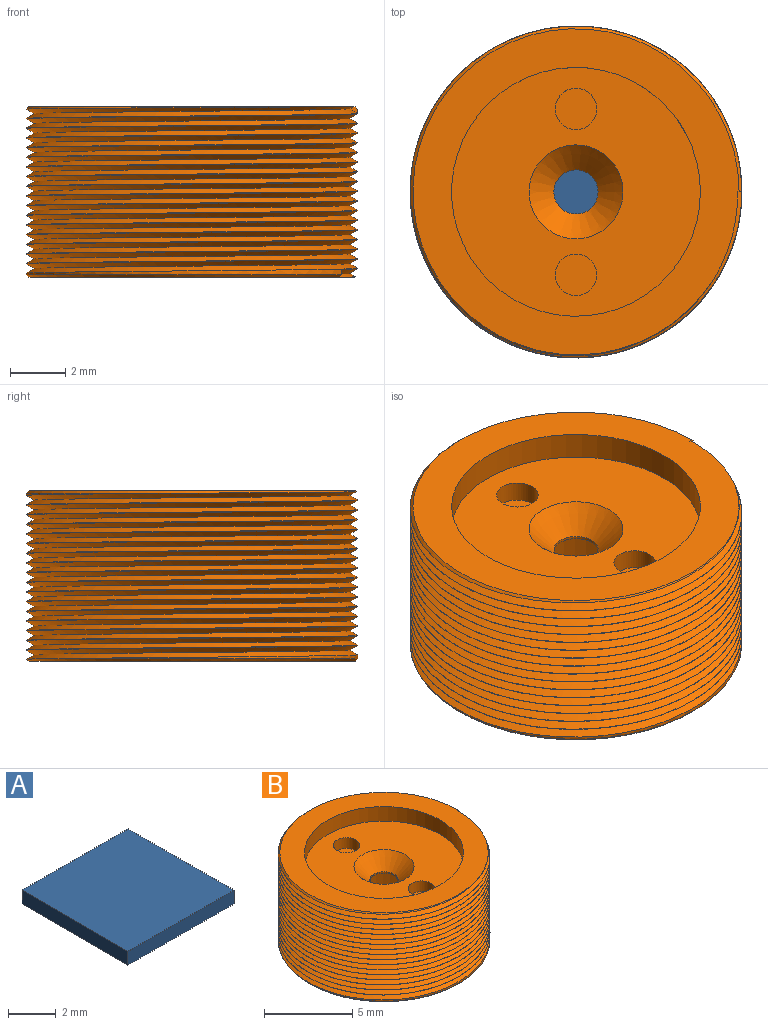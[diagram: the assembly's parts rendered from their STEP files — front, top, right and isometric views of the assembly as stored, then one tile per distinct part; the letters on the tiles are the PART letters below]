
ASSEMBLY  parts=2 mates=1
PART A: 6 faces, bbox 6.3x6.3x0.7 mm
  f0: plane 6.25x0.7mm, normal (0,-1,0), area 4.4mm2, adj f1,f3,f4,f5
  f1: plane 6.25x0.7mm, normal (1,0,0), area 4.4mm2, adj f0,f2,f4,f5
  f2: plane 6.25x0.7mm, normal (0,1,0), area 4.4mm2, adj f1,f3,f4,f5
  f3: plane 6.25x0.7mm, normal (-1,0,0), area 4.4mm2, adj f0,f2,f4,f5
  f4: plane 6.25x6.25mm, normal (0,0,1), area 39.1mm2, adj f0,f1,f2,f3
  f5: plane 6.25x6.25mm, normal (0,0,-1), area 39.1mm2, adj f0,f1,f2,f3
PART B: 21 faces, bbox 12.1x13.9x6.4 mm
  f0: cylinder r=6mm len=12mm, axis (0,0,-1), area 9.1mm2, adj f2,f12,f17,f18,f19,f20
  f1: plane 11.87x11.87mm, normal (0,0,1), area 45.6mm2, adj f2,f4,f17,f20
  f2: cone r=5.9mm half-angle=45deg, axis (0,0,-1), area 3.6mm2, adj f0,f1,f17,f20
  f3: plane 9x9mm, normal (0,0,1), area 51mm2, adj f4,f11,f13,f15
  f4: cylinder r=4.5mm len=9mm, axis (0,0,-1), area 28.3mm2, adj f1,f3
  f5: cylinder r=5mm len=10mm, axis (0,0,1), area 31.4mm2, adj f6,f9
  f6: plane 11.8x11.8mm, normal (0,0,-1), area 30.8mm2, adj f5,f12
  f7: plane 6.5x6.5mm, normal (0,0,-1), area 31.2mm2, adj f8,f10
  f8: cylinder r=3.25mm len=6.5mm, axis (0,0,1), area 64.8mm2, adj f7,f9
  f9: plane 10x10mm, normal (0,0,-1), area 45.4mm2, adj f5,f8
  f10: cylinder r=0.8mm len=1.6mm, axis (0,0,1), area 0.5mm2, adj f7,f11
  f11: cone r=0.8mm half-angle=45deg, axis (0,0,1), area 10mm2, adj f3,f10
  f12: cone r=6mm half-angle=45deg, axis (0,0,1), area 4.2mm2, adj f0,f6,f18,f19
  f13: cylinder r=0.75mm len=1.5mm, axis (0,0,1), area 3.5mm2, adj f3,f14
  f14: plane 1.5x1.5mm, normal (0,0,1), area 1.8mm2, adj f13
  f15: cylinder r=0.75mm len=1.5mm, axis (0,0,1), area 3.5mm2, adj f3,f16
  f16: plane 1.5x1.5mm, normal (0,0,1), area 1.8mm2, adj f15
  f17: plane 0.29x0.25mm, normal (0,-1,0), area 0mm2, adj f0,f1,f2,f19,f20
  f18: plane 0.29x0.27mm, normal (0.43,0.9,0), area 0mm2, adj f0,f12,f19,f20
  f19: bspline ~13.86x12mm, area 217.2mm2, adj f0,f12,f17,f18,f20
  f20: bspline ~13.86x12mm, area 212.1mm2, adj f0,f1,f2,f17,f18,f19
PLACE A t=(2.82,5.55,-5.81)mm
PLACE B t=(2.82,5.55,-1.94)mm
MATE planar B.f5 <-> A.f4  axis (0,0,-1) through (2.82,5.55,-5.11)mm
